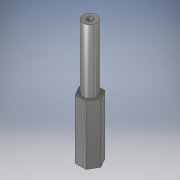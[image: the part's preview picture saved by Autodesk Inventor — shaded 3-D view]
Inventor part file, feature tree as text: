
AUTODESK INVENTOR PART (.ipt)
format: ipt  version: 2017 SP1 (Build 210196100, 196)  size: 116,736 bytes
history: native  units: in
note: dims shown in document units (in); Inventor stores cm internally (conversion verified against a paired STEP export)
features: extrude x4, sketch x4
ambient origin geometry x8: Origin, YZ Plane, XZ Plane, XY Plane, X Axis, Y Axis, Z Axis, Center Point
bodies: Solid1 (feature_tree)
feature tree (8):
  extrude  "Extrusion1"  Depth=1.5625in TaperAngle=0.0deg
  extrude  "Extrusion2"  Depth=1.6875in TaperAngle=0.0deg
  extrude  "Extrusion3"  Depth=1.0in TaperAngle=0.0deg
  extrude  "Extrusion4"  [1 undecoded]
  sketch  "Sketch1"  dims[d0=0.5in d1=1.5625in d2=0.0in]
  sketch  "Sketch2"  dims[d3=0.375in d4=1.6875in d5=0.0in]
  sketch  "Sketch3"  dims[d7=0.15in d8=1.0in d9=0.0in]
  sketch  "Sketch4"  dims[d10=1.0in d11=0.0in]
note: 1 required parameter value undecoded (feature->parameter linkage not recoverable at this tier; creation-order binding heuristic only, values carry confidence <= 0.55)
